# Revit family: Lighting-Track-Reggiani-Yori_95mm-30W
name_source: partatom
category: Apparecchi per illuminazione
revit_build: Autodesk Revit 2015 (Build: 20140323_1530(x64)
units: mm (PartAtom-declared; Revit-internal decimal feet)

## types (2) — shared parameters
Angolo inclinazione = 90.00°
BIMobject category = Lighting
Box internal = Reggiani Nero
Data Sheet = http://www.reggiani.net
Date of publishing = 2015-10-01
Descrizione = Minimalism and rigour in the service of functionality, Yori is a high performance luminaire with a compact footprint. Two simple bodies combined by a simple joint allow the optical section to be adjusted. Yori is designed for the most innovative LED and metal halide lamps, and is configured for mounting on tracks, inside channels, recessed, onto surfaces and inside grooves in ceilings, thanks to the new versi ...
Design country = Italy
Edition number = 1
File diagramma fotometrico = TD97B_HW_30W_15degrees beam_LED 2767lm_2700K_cri 90.ies
Filtro dei colori = 16777215
IFC Classification = Light Fixture
Installation instructions = http://www.reggiani.net
Lampada = Led
Lens = Lente Yori polic trasparente
Lens frame = Reggiani Nero
Manufacturer country = Italy
Manufacturer name = Reggiani
Material main = Aluminium
Material secondary = Glass
Modello = Reggiani Yori  TD 97
Nominal height = 135
Nominal width = 95
Product Guid = 6c2995b9-41c6-4809-92bb-273245acc23c
Product SKU = yori_track_95
Product data url = http://bimobject.com
Product family = Track fixture
Product group = Yori
Produttore = Reggiani illuminazione spa
QR code = http://bimobject.com
Ring = Reggiani Nero
Technical description = http://www.reggiani.net
UNSPSC Code = 3911
URL = http://www.reggiani.net
URL to photometrics = http://bimobject.com
Variazione temperatura colore lampada con luminosità attenuata = <Nessuno>
Weight Net (Kg) = 1.17
control = Ø. = ON/OFF, D. = DALI, V. = DIMM 1-10V, T

## per-type parameters (varying)
| type | Box closed | Docking | Docking up | UNSPSC name |
| Reggiani Yori TD97 white 30 w | Reggiani Bianco | Reggiani Bianco | Reggiani Bianco | Lighting Fixtures and Accessories |
| Reggiani Yori TD97 Black  30w | Reggiani Nero | Reggiani Nero | Reggiani Nero |  |

## geometry (parser evidence)
native form markers: Blend x8
no freeform markers — native parametric forms only
